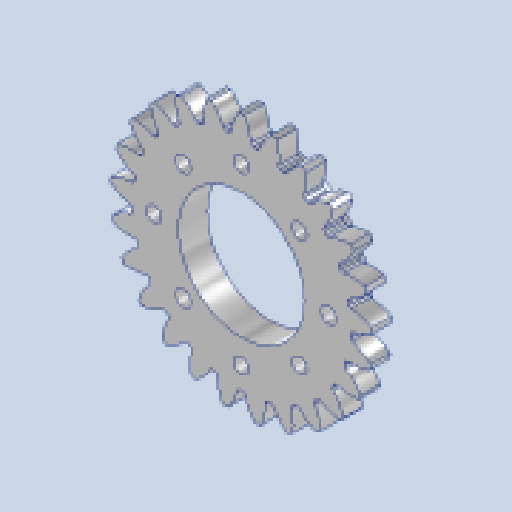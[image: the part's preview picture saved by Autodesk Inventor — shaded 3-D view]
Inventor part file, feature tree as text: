
AUTODESK INVENTOR PART (.ipt)
format: ipt  version: 2023.1 (Build 271208000, 208)  size: 382,976 bytes
history: native  units: mm
features: extrude x3, sketch x3, other x1, pattern_circular x1, projected_geometry x1
ambient origin geometry x8: Origin, YZ Plane, XZ Plane, XY Plane, X Axis, Y Axis, Z Axis, Center Point
bodies: Body1 (feature_tree)
feature tree (9):
  other  "솔리드1"
  extrude  "돌출1"  Depth=50.0mm
  pattern_circular  "원형 패턴1"  [2 undecoded]
  extrude  "돌출2"  Depth=4.5mm
  extrude  "돌출3"  Depth=0.5mm
  sketch  "스케치1"
  sketch  "스케치2"
  sketch  "스케치3"
  projected_geometry  "투영된 루프1"
note: 2 required parameter values undecoded (feature->parameter linkage not recoverable at this tier; creation-order binding heuristic only, values carry confidence <= 0.55)
